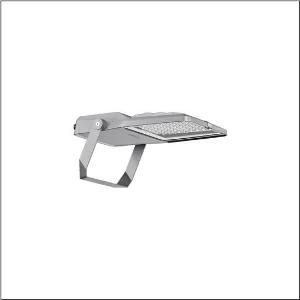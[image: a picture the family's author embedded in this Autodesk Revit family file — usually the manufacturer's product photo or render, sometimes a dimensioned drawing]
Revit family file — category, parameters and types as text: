
# Revit family: floodlight_fl_21_mini___pl52_5xa7773c2d1a_dd61
name_source: partatom
category: Lighting Fixtures
units: mm (PartAtom-declared; Revit-internal decimal feet)

## family parameters
Cut with Voids When Loaded = No
Host = Face
Light Source = No
Part Type = Normal
Room Calculation Point = No
Round Connector Dimension = Use Diameter
Shared = No

## types (1)
- --- (1 x LED, 19510 lm, 163.5 W, 3000K)
    Apparent Load = 163 VA
    CIE Flux Codes = 26 60 98 100 100
    Color Rendering = 70
    Color Temperature = 3000K
    Default Elevation = 1800 mm
    Description = Floodlight FL 21 mini, floodlight, primary light control with lens, of PMMA, primary optical cover: protective disc, of toughened safety glass, transparent, light distribution: PL52, light emission: direct distribution, installation type: surface-mounted, LED, High Power LED, rated luminous flux: 19.510lm, luminous efficacy: 119lm/W, light colour: 730, colour temperature: 3000K, control: Temp-Guard, with terminal, 6-pole, mains connection: 220..240V, AC, 50/60Hz, start of lifetime: 164W, luminaire housing, of diecast aluminium, powder-coated, Siteco® metallic grey (DB 702S), corrosivity category C5 mid according to DIN EN ISO 12944, sealing non-destructively replaceable, mounting bracket, of steel, galvanised, powder-coated, Siteco® metallic grey (DB 702S), ON/OFF, protection rating (complete): IP66, insulation class (complete): insulation class I (protective earthing), certification: CE, ENEC, VDE, protection symbol: D, impact resistance: IK08, permissible operating ambient temperature: -40..+40°C, permissible operating ambient temperature for outdoor applications: -40..+50°C, standard: DIN EN 12944, LABS conformity tested according to VDMA 24364:2018-05, packaging unit: 1 piece

Light Distribution: PL52
    Height = 70 mm
    Lamp = 1 x LED
    Lamp Light Flux = 19510 lm
    Lamp Power = 163.5 W
    Lamp count = 1
    Length = 485 mm
    Luminous efficacy = 119 lm/W
    Manufacturer = Siteco
    ModVariant = No
    Model = 5XA7773C2D1A
    Number of Poles = 1
    OnlyDefault = Yes
    Power Factor = 1
    Product Name = Floodlight FL 21 mini | PL52
    Product group = floodlight | pylon annexe
    ProductGroupID = 6200
    Protection Class = Protection class I
    Protection Degree = IP 66
    RLX_Detail_Level = 1
    RLX_Emergency_Light_Flux = 0 lm
    RLX_Emergency_Type = 0
    RLX_Emergency_Type_DB = No
    RlxData = <blob elided: 94261 chars, md5=6b1c330c>
    Socket = socket
    Standby Power = 0 W
    System Light Flux = 19510 lm
    System Power = 163 W
    Type Comments = factory setting: luminous flux: 100 % | (ON | - | - | - | - | - | - | -) | 825 mA
    Type Image = l_1006845.jpg
    URL = http://relux.com
    VarID = @adj_096407
    Voltage = 0 V
    Weight = 0.00 kg
    Width = 337 mm

## geometry (parser evidence)
native form markers: Blend x4, Sweep x12
no freeform markers — native parametric forms only
